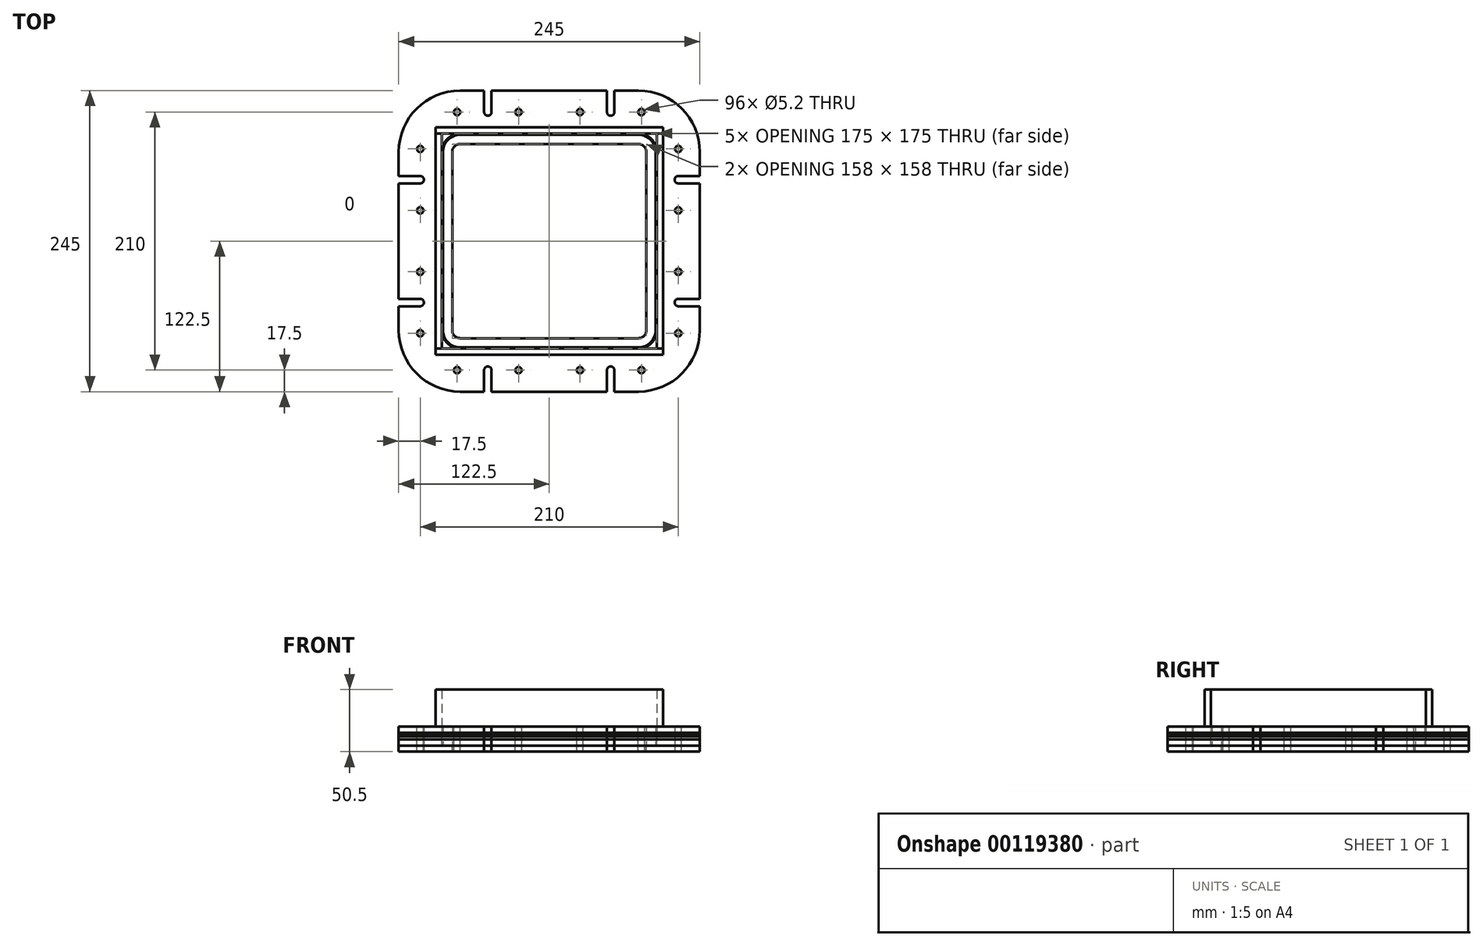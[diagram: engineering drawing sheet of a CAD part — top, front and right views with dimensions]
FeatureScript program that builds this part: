
annotation { "Feature Type Name" : "Feature", "Feature Type Description" : "" }
export const myFeature = defineFeature(function(context is Context, id is Id, definition is map)
    precondition{}
    {
        {
            var Q0;
            Q0=qCreatedBy(makeId("Top.planeOp"),FACE);
            var sketch = newSketch(context, id + "F0", { "sketchPlane" : qUnion([Q0])});
            skLineSegment(sketch, "E0.bottom", {"start": v(72.5, -87.5) * mm, "end": v(-72.5, -87.5) * mm});
            skLineSegment(sketch, "E0.top", {"start": v(72.5, 87.5) * mm, "end": v(-72.5, 87.5) * mm});
            skLineSegment(sketch, "E0.left", {"start": v(87.5, -72.5) * mm, "end": v(87.5, 72.5) * mm});
            skLineSegment(sketch, "E0.right", {"start": v(-87.5, -72.5) * mm, "end": v(-87.5, 72.5) * mm});
            skPoint(sketch, "E0.middle", {"position": v(0, 0) * mm});
            skPoint(sketch, "E1.visualSharp", {"position": v(-87.5, 87.5) * mm});
            skArc(sketch, "E1.filletArc", {"start": v(-72.5, 87.5) * mm, "mid": v(-83.1, 83.1) * mm, "end": v(-87.5, 72.5) * mm});
            skPoint(sketch, "E2.visualSharp", {"position": v(87.5, 87.5) * mm});
            skArc(sketch, "E2.filletArc", {"start": v(87.5, 72.5) * mm, "mid": v(83.1, 83.1) * mm, "end": v(72.5, 87.5) * mm});
            skPoint(sketch, "E3.visualSharp", {"position": v(87.5, -87.5) * mm});
            skArc(sketch, "E3.filletArc", {"start": v(72.5, -87.5) * mm, "mid": v(83.1, -83.1) * mm, "end": v(87.5, -72.5) * mm});
            skPoint(sketch, "E4.visualSharp", {"position": v(-87.5, -87.5) * mm});
            skArc(sketch, "E4.filletArc", {"start": v(-87.5, -72.5) * mm, "mid": v(-83.1, -83.1) * mm, "end": v(-72.5, -87.5) * mm});
            skArc(sketch, "E5.0", {"start": v(72.5, -122.5) * mm, "mid": v(107.86, -107.86) * mm, "end": v(122.5, -72.5) * mm});
            skLineSegment(sketch, "E5.1", {"start": v(72.5, -122.5) * mm, "end": v(-72.5, -122.5) * mm});
            skLineSegment(sketch, "E5.2", {"start": v(122.5, -72.5) * mm, "end": v(122.5, 72.5) * mm});
            skArc(sketch, "E5.3", {"start": v(-122.5, -72.5) * mm, "mid": v(-107.86, -107.86) * mm, "end": v(-72.5, -122.5) * mm});
            skArc(sketch, "E5.4", {"start": v(122.5, 72.5) * mm, "mid": v(107.86, 107.86) * mm, "end": v(72.5, 122.5) * mm});
            skLineSegment(sketch, "E5.5", {"start": v(72.5, 122.5) * mm, "end": v(-72.5, 122.5) * mm});
            skArc(sketch, "E5.6", {"start": v(-72.5, 122.5) * mm, "mid": v(-107.86, 107.86) * mm, "end": v(-122.5, 72.5) * mm});
            skLineSegment(sketch, "E5.7", {"start": v(-122.5, -72.5) * mm, "end": v(-122.5, 72.5) * mm});
            skSolve(sketch);
        }
        {
            var Q0;
            Q0=makeQuery(id+"F0.imprint","IMPRINT",FACE,{"disambiguationData":[TD([[makeQuery(id+"F0.imprint","IMPRINT",EDGE,{"derivedFrom":sQuery(id+"F0.wireOp",EDGE,"E0.bottom")}),1.0]])]});
            extrude(context, id + "F1", {"entities" : qUnion([Q0]), "depth" : 5 * mm});
        }
        {
            var Q0;
            Q0=makeQuery(id+"F1.opExtrude","CAP_FACE",FACE,{"disambiguationData":[OSD([sQuery(id+"F0.wireOp",EDGE,"E0.bottom"),sQuery(id+"F0.wireOp",EDGE,"E0.top"),sQuery(id+"F0.wireOp",EDGE,"E0.left"),sQuery(id+"F0.wireOp",EDGE,"E0.right"),sQuery(id+"F0.wireOp",EDGE,"E1.filletArc"),sQuery(id+"F0.wireOp",EDGE,"E2.filletArc"),sQuery(id+"F0.wireOp",EDGE,"E3.filletArc"),sQuery(id+"F0.wireOp",EDGE,"E4.filletArc"),sQuery(id+"F0.wireOp",EDGE,"E5.0"),sQuery(id+"F0.wireOp",EDGE,"E5.1"),sQuery(id+"F0.wireOp",EDGE,"E5.2"),sQuery(id+"F0.wireOp",EDGE,"E5.3"),sQuery(id+"F0.wireOp",EDGE,"E5.4"),sQuery(id+"F0.wireOp",EDGE,"E5.5"),sQuery(id+"F0.wireOp",EDGE,"E5.6"),sQuery(id+"F0.wireOp",EDGE,"E5.7")])],"isStart":true});
            var sketch = newSketch(context, id + "F2", { "sketchPlane" : qUnion([Q0])});
            skArc(sketch, "E6", {"start": v(72.5, 87.5) * mm, "mid": v(83.1, 83.1) * mm, "end": v(87.5, 72.5) * mm});
            skLineSegment(sketch, "E7", {"start": v(72.5, 87.5) * mm, "end": v(-72.5, 87.5) * mm});
            skArc(sketch, "E8", {"start": v(-87.5, 72.5) * mm, "mid": v(-83.1, 83.1) * mm, "end": v(-72.5, 87.5) * mm});
            skLineSegment(sketch, "E9", {"start": v(-87.5, 72.5) * mm, "end": v(-87.5, -72.5) * mm});
            skArc(sketch, "E10", {"start": v(-72.5, -87.5) * mm, "mid": v(-83.1, -83.1) * mm, "end": v(-87.5, -72.5) * mm});
            skLineSegment(sketch, "E11", {"start": v(72.5, -87.5) * mm, "end": v(-72.5, -87.5) * mm});
            skArc(sketch, "E12", {"start": v(87.5, -72.5) * mm, "mid": v(83.1, -83.1) * mm, "end": v(72.5, -87.5) * mm});
            skLineSegment(sketch, "E13", {"start": v(87.5, 72.5) * mm, "end": v(87.5, -72.5) * mm});
            skArc(sketch, "E14", {"start": v(-122.5, 72.5) * mm, "mid": v(-107.86, 107.86) * mm, "end": v(-72.5, 122.5) * mm});
            skLineSegment(sketch, "E15", {"start": v(-122.5, 72.5) * mm, "end": v(-122.5, -72.5) * mm});
            skArc(sketch, "E16", {"start": v(-72.5, -122.5) * mm, "mid": v(-107.86, -107.86) * mm, "end": v(-122.5, -72.5) * mm});
            skLineSegment(sketch, "E17", {"start": v(72.5, -122.5) * mm, "end": v(-72.5, -122.5) * mm});
            skArc(sketch, "E18", {"start": v(122.5, -72.5) * mm, "mid": v(107.86, -107.86) * mm, "end": v(72.5, -122.5) * mm});
            skLineSegment(sketch, "E19", {"start": v(122.5, 72.5) * mm, "end": v(122.5, -72.5) * mm});
            skArc(sketch, "E20", {"start": v(72.5, 122.5) * mm, "mid": v(107.86, 107.86) * mm, "end": v(122.5, 72.5) * mm});
            skLineSegment(sketch, "E21", {"start": v(72.5, 122.5) * mm, "end": v(-72.5, 122.5) * mm});
            skSolve(sketch);
        }
        {
            var Q0;
            Q0=makeQuery(id+"F2.imprint","IMPRINT",FACE,{"disambiguationData":[TD([[makeQuery(id+"F2.imprint","IMPRINT",EDGE,{"derivedFrom":sQuery(id+"F2.wireOp",EDGE,"41d78850-efe2-4f69-8b8e-5f8f88f08fe800")}),1.0]])]});
            var Q1;
            Q1=makeQuery(id+"F2.imprint","IMPRINT",FACE,{"disambiguationData":[TD([[makeQuery(id+"F2.imprint","IMPRINT",EDGE,{"derivedFrom":sQuery(id+"F2.wireOp",EDGE,"E6")}),1.0]])]});
            extrude(context, id + "F3", {"entities" : qUnion([Q0, Q1]), "depth" : 2.5 * mm});
        }
        {
            var Q0;
            Q0=makeQuery(id+"F1.opExtrude","CAP_FACE",FACE,{"disambiguationData":[OSD([sQuery(id+"F0.wireOp",EDGE,"E0.bottom"),sQuery(id+"F0.wireOp",EDGE,"E0.top"),sQuery(id+"F0.wireOp",EDGE,"E0.left"),sQuery(id+"F0.wireOp",EDGE,"E0.right"),sQuery(id+"F0.wireOp",EDGE,"E1.filletArc"),sQuery(id+"F0.wireOp",EDGE,"E2.filletArc"),sQuery(id+"F0.wireOp",EDGE,"E3.filletArc"),sQuery(id+"F0.wireOp",EDGE,"E4.filletArc"),sQuery(id+"F0.wireOp",EDGE,"E5.0"),sQuery(id+"F0.wireOp",EDGE,"E5.1"),sQuery(id+"F0.wireOp",EDGE,"E5.2"),sQuery(id+"F0.wireOp",EDGE,"E5.3"),sQuery(id+"F0.wireOp",EDGE,"E5.4"),sQuery(id+"F0.wireOp",EDGE,"E5.5"),sQuery(id+"F0.wireOp",EDGE,"E5.6"),sQuery(id+"F0.wireOp",EDGE,"E5.7")])],"isStart":false});
            var sketch = newSketch(context, id + "F4", { "sketchPlane" : qUnion([Q0])});
            skLineSegment(sketch, "E22.bottom", {"start": v(-92.5, -87.5) * mm, "end": v(92.5, -87.5) * mm});
            skLineSegment(sketch, "E22.top", {"start": v(-92.5, 87.5) * mm, "end": v(92.5, 87.5) * mm});
            skLineSegment(sketch, "E22.left", {"start": v(-87.5, -87.5) * mm, "end": v(-87.5, 87.5) * mm});
            skLineSegment(sketch, "E22.right", {"start": v(87.5, -87.5) * mm, "end": v(87.5, 87.5) * mm});
            skPoint(sketch, "E22.middle", {"position": v(0, 0) * mm});
            skLineSegment(sketch, "E23.0", {"start": v(-92.5, -92.5) * mm, "end": v(92.5, -92.5) * mm});
            skLineSegment(sketch, "E23.1", {"start": v(-92.5, -92.5) * mm, "end": v(-92.5, 92.5) * mm});
            skLineSegment(sketch, "E23.2", {"start": v(-92.5, 92.5) * mm, "end": v(92.5, 92.5) * mm});
            skLineSegment(sketch, "E23.3", {"start": v(92.5, -92.5) * mm, "end": v(92.5, 92.5) * mm});
            skSolve(sketch);
        }
        {
            var Q0;
            {var subQ5=sQuery(id+"F4.wireOp",EDGE,"E23.2");Q0=makeQuery(id+"F4.imprint","IMPRINT",FACE,{"disambiguationData":[TD([[makeQuery(id+"F4.imprint","IMPRINT",EDGE,{"derivedFrom":subQ5}),-1.0]])]});}
            var Q1;
            {var subQ4=sQuery(id+"F4.wireOp",EDGE,"E23.0");Q1=makeQuery(id+"F4.imprint","IMPRINT",FACE,{"disambiguationData":[TD([[makeQuery(id+"F4.imprint","IMPRINT",EDGE,{"derivedFrom":subQ4}),1.0]])]});}
            extrude(context, id + "F5", {"entities" : qUnion([Q0, Q1]), "depth" : 30 * mm});
        }
        {
            var Q0;
            Q0=makeQuery(id+"F1.opExtrude","CAP_FACE",FACE,{"disambiguationData":[OSD([sQuery(id+"F0.wireOp",EDGE,"E0.bottom"),sQuery(id+"F0.wireOp",EDGE,"E0.top"),sQuery(id+"F0.wireOp",EDGE,"E0.left"),sQuery(id+"F0.wireOp",EDGE,"E0.right"),sQuery(id+"F0.wireOp",EDGE,"E1.filletArc"),sQuery(id+"F0.wireOp",EDGE,"E2.filletArc"),sQuery(id+"F0.wireOp",EDGE,"E3.filletArc"),sQuery(id+"F0.wireOp",EDGE,"E4.filletArc"),sQuery(id+"F0.wireOp",EDGE,"E5.0"),sQuery(id+"F0.wireOp",EDGE,"E5.1"),sQuery(id+"F0.wireOp",EDGE,"E5.2"),sQuery(id+"F0.wireOp",EDGE,"E5.3"),sQuery(id+"F0.wireOp",EDGE,"E5.4"),sQuery(id+"F0.wireOp",EDGE,"E5.5"),sQuery(id+"F0.wireOp",EDGE,"E5.6"),sQuery(id+"F0.wireOp",EDGE,"E5.7")])],"isStart":false});
            var sketch = newSketch(context, id + "F6", { "sketchPlane" : qUnion([Q0])});
            skLineSegment(sketch, "E24.bottom", {"start": v(87.5, 87.5) * mm, "end": v(92.5, 87.5) * mm});
            skLineSegment(sketch, "E24.top", {"start": v(87.5, -87.5) * mm, "end": v(92.5, -87.5) * mm});
            skLineSegment(sketch, "E24.left", {"start": v(87.5, 87.5) * mm, "end": v(87.5, -87.5) * mm});
            skLineSegment(sketch, "E24.right", {"start": v(92.5, 87.5) * mm, "end": v(92.5, -87.5) * mm});
            skLineSegment(sketch, "E25.bottom", {"start": v(-87.5, 87.5) * mm, "end": v(-92.5, 87.5) * mm});
            skLineSegment(sketch, "E25.top", {"start": v(-87.5, -87.5) * mm, "end": v(-92.5, -87.5) * mm});
            skLineSegment(sketch, "E25.left", {"start": v(-87.5, 87.5) * mm, "end": v(-87.5, -87.5) * mm});
            skLineSegment(sketch, "E25.right", {"start": v(-92.5, 87.5) * mm, "end": v(-92.5, -87.5) * mm});
            skSolve(sketch);
        }
        {
            var Q0;
            {var subQ3=sQuery(id+"F6.wireOp",EDGE,"E25.bottom");Q0=makeQuery(id+"F6.imprint","IMPRINT",FACE,{"disambiguationData":[TD([[makeQuery(id+"F6.imprint","IMPRINT",EDGE,{"derivedFrom":subQ3}),1.0]])]});}
            var Q1;
            {var subQ4=sQuery(id+"F6.wireOp",EDGE,"E24.bottom");Q1=makeQuery(id+"F6.imprint","IMPRINT",FACE,{"disambiguationData":[TD([[makeQuery(id+"F6.imprint","IMPRINT",EDGE,{"derivedFrom":subQ4}),-1.0]])]});}
            extrude(context, id + "F7", {"entities" : qUnion([Q0, Q1]), "depth" : 30 * mm});
        }
        {
            var Q0;
            Q0=makeQuery(id+"F3.opExtrude","CAP_FACE",FACE,{"disambiguationData":[OSD([sQuery(id+"F2.wireOp",EDGE,"E6"),sQuery(id+"F2.wireOp",EDGE,"E7"),sQuery(id+"F2.wireOp",EDGE,"E8"),sQuery(id+"F2.wireOp",EDGE,"E9"),sQuery(id+"F2.wireOp",EDGE,"E10"),sQuery(id+"F2.wireOp",EDGE,"E11"),sQuery(id+"F2.wireOp",EDGE,"E12"),sQuery(id+"F2.wireOp",EDGE,"E13"),sQuery(id+"F2.wireOp",EDGE,"E14"),sQuery(id+"F2.wireOp",EDGE,"E15"),sQuery(id+"F2.wireOp",EDGE,"E16"),sQuery(id+"F2.wireOp",EDGE,"E17"),sQuery(id+"F2.wireOp",EDGE,"E18"),sQuery(id+"F2.wireOp",EDGE,"E19"),sQuery(id+"F2.wireOp",EDGE,"E20"),sQuery(id+"F2.wireOp",EDGE,"E21")])],"isStart":false});
            extrude(context, id + "F8", {"entities" : qUnion([Q0]), "depth" : .5 * mm});
        }
        {
            var Q0;
            Q0=makeQuery(id+"F8.opExtrude","CAP_FACE",FACE,{"disambiguationData":[OSD([sQuery(id+"F2.wireOp",EDGE,"E6"),sQuery(id+"F2.wireOp",EDGE,"E7"),sQuery(id+"F2.wireOp",EDGE,"E8"),sQuery(id+"F2.wireOp",EDGE,"E9"),sQuery(id+"F2.wireOp",EDGE,"E10"),sQuery(id+"F2.wireOp",EDGE,"E11"),sQuery(id+"F2.wireOp",EDGE,"E12"),sQuery(id+"F2.wireOp",EDGE,"E13"),sQuery(id+"F2.wireOp",EDGE,"E14"),sQuery(id+"F2.wireOp",EDGE,"E15"),sQuery(id+"F2.wireOp",EDGE,"E16"),sQuery(id+"F2.wireOp",EDGE,"E17"),sQuery(id+"F2.wireOp",EDGE,"E18"),sQuery(id+"F2.wireOp",EDGE,"E19"),sQuery(id+"F2.wireOp",EDGE,"E20"),sQuery(id+"F2.wireOp",EDGE,"E21")])],"isStart":false});
            extrude(context, id + "F9", {"entities" : qUnion([Q0]), "depth" : 2.5 * mm});
        }
        {
            var Q0;
            Q0=makeQuery(id+"F9.opExtrude","CAP_FACE",FACE,{"disambiguationData":[OSD([sQuery(id+"F2.wireOp",EDGE,"E6"),sQuery(id+"F2.wireOp",EDGE,"E7"),sQuery(id+"F2.wireOp",EDGE,"E8"),sQuery(id+"F2.wireOp",EDGE,"E9"),sQuery(id+"F2.wireOp",EDGE,"E10"),sQuery(id+"F2.wireOp",EDGE,"E11"),sQuery(id+"F2.wireOp",EDGE,"E12"),sQuery(id+"F2.wireOp",EDGE,"E13"),sQuery(id+"F2.wireOp",EDGE,"E14"),sQuery(id+"F2.wireOp",EDGE,"E15"),sQuery(id+"F2.wireOp",EDGE,"E16"),sQuery(id+"F2.wireOp",EDGE,"E17"),sQuery(id+"F2.wireOp",EDGE,"E18"),sQuery(id+"F2.wireOp",EDGE,"E19"),sQuery(id+"F2.wireOp",EDGE,"E20"),sQuery(id+"F2.wireOp",EDGE,"E21")])],"isStart":false});
            extrude(context, id + "F10", {"entities" : qUnion([Q0]), "depth" : 5 * mm});
        }
        {
            var Q0;
            Q0=makeQuery(id+"F10.opExtrude","CAP_FACE",FACE,{"disambiguationData":[OSD([sQuery(id+"F2.wireOp",EDGE,"E6"),sQuery(id+"F2.wireOp",EDGE,"E7"),sQuery(id+"F2.wireOp",EDGE,"E8"),sQuery(id+"F2.wireOp",EDGE,"E9"),sQuery(id+"F2.wireOp",EDGE,"E10"),sQuery(id+"F2.wireOp",EDGE,"E11"),sQuery(id+"F2.wireOp",EDGE,"E12"),sQuery(id+"F2.wireOp",EDGE,"E13"),sQuery(id+"F2.wireOp",EDGE,"E14"),sQuery(id+"F2.wireOp",EDGE,"E15"),sQuery(id+"F2.wireOp",EDGE,"E16"),sQuery(id+"F2.wireOp",EDGE,"E17"),sQuery(id+"F2.wireOp",EDGE,"E18"),sQuery(id+"F2.wireOp",EDGE,"E19"),sQuery(id+"F2.wireOp",EDGE,"E20"),sQuery(id+"F2.wireOp",EDGE,"E21")])],"isStart":false});
            var sketch = newSketch(context, id + "F11", { "sketchPlane" : qUnion([Q0])});
            skLineSegment(sketch, "E26.0", {"start": v(72.5, 86.5) * mm, "end": v(-72.5, 86.5) * mm});
            skArc(sketch, "E26.1", {"start": v(-86.5, 72.5) * mm, "mid": v(-82.4, 82.4) * mm, "end": v(-72.5, 86.5) * mm});
            skArc(sketch, "E26.2", {"start": v(72.5, 86.5) * mm, "mid": v(82.4, 82.4) * mm, "end": v(86.5, 72.5) * mm});
            skLineSegment(sketch, "E26.3", {"start": v(-86.5, 72.5) * mm, "end": v(-86.5, -72.5) * mm});
            skLineSegment(sketch, "E26.4", {"start": v(86.5, 72.5) * mm, "end": v(86.5, -72.5) * mm});
            skArc(sketch, "E26.5", {"start": v(86.5, -72.5) * mm, "mid": v(82.4, -82.4) * mm, "end": v(72.5, -86.5) * mm});
            skLineSegment(sketch, "E26.6", {"start": v(72.5, -86.5) * mm, "end": v(-72.5, -86.5) * mm});
            skArc(sketch, "E26.7", {"start": v(-72.5, -86.5) * mm, "mid": v(-82.4, -82.4) * mm, "end": v(-86.5, -72.5) * mm});
            skLineSegment(sketch, "E27.0", {"start": v(72.5, 79) * mm, "end": v(-72.5, 79) * mm});
            skArc(sketch, "E27.1", {"start": v(-79, 72.5) * mm, "mid": v(-77.1, 77.1) * mm, "end": v(-72.5, 79) * mm});
            skArc(sketch, "E27.2", {"start": v(72.5, 79) * mm, "mid": v(77.1, 77.1) * mm, "end": v(79, 72.5) * mm});
            skLineSegment(sketch, "E27.3", {"start": v(-79, 72.5) * mm, "end": v(-79, -72.5) * mm});
            skLineSegment(sketch, "E27.4", {"start": v(79, 72.5) * mm, "end": v(79, -72.5) * mm});
            skArc(sketch, "E27.5", {"start": v(79, -72.5) * mm, "mid": v(77.1, -77.1) * mm, "end": v(72.5, -79) * mm});
            skLineSegment(sketch, "E27.6", {"start": v(72.5, -79) * mm, "end": v(-72.5, -79) * mm});
            skArc(sketch, "E27.7", {"start": v(-72.5, -79) * mm, "mid": v(-77.1, -77.1) * mm, "end": v(-79, -72.5) * mm});
            skLineSegment(sketch, "E28.0", {"start": v(72.5, 122.5) * mm, "end": v(-72.5, 122.5) * mm});
            skArc(sketch, "E29.0", {"start": v(-122.5, 72.5) * mm, "mid": v(-107.86, 107.86) * mm, "end": v(-72.5, 122.5) * mm});
            skLineSegment(sketch, "E30.0", {"start": v(-122.5, 72.5) * mm, "end": v(-122.5, -72.5) * mm});
            skArc(sketch, "E31.0", {"start": v(-72.5, -122.5) * mm, "mid": v(-107.86, -107.86) * mm, "end": v(-122.5, -72.5) * mm});
            skLineSegment(sketch, "E32.0", {"start": v(72.5, -122.5) * mm, "end": v(-72.5, -122.5) * mm});
            skArc(sketch, "E33.0", {"start": v(122.5, -72.5) * mm, "mid": v(107.86, -107.86) * mm, "end": v(72.5, -122.5) * mm});
            skLineSegment(sketch, "E34.0", {"start": v(122.5, 72.5) * mm, "end": v(122.5, -72.5) * mm});
            skArc(sketch, "E35.0", {"start": v(72.5, 122.5) * mm, "mid": v(107.86, 107.86) * mm, "end": v(122.5, 72.5) * mm});
            skSolve(sketch);
        }
        {
            var Q0;
            Q0=makeQuery(id+"F11.imprint","IMPRINT",FACE,{"disambiguationData":[TD([[makeQuery(id+"F11.imprint","IMPRINT",EDGE,{"derivedFrom":sQuery(id+"F11.wireOp",EDGE,"E26.0")}),1.0]])]});
            extrude(context, id + "F12", {"entities" : qUnion([Q0]), "oppositeDirection" : true, "depth" : 15 * mm});
        }
        {
            var Q0;
            Q0 = qSketchRegion(id + "F11", true);
            var Q1;
            Q1=makeQuery(id+"F11.imprint","IMPRINT",FACE,{"disambiguationData":[TD([[makeQuery(id+"F11.imprint","IMPRINT",EDGE,{"derivedFrom":sQuery(id+"F11.wireOp",EDGE,"E26.0")}),1.0]])]});
            extrude(context, id + "F13", {"entities" : qUnion([Q0, Q1]), "depth" : 5 * mm});
        }
        {
            var Q0;
            Q0=makeQuery(id+"F13.opExtrude","CAP_FACE",FACE,{"disambiguationData":[OSD([sQuery(id+"F11.wireOp",EDGE,"E27.0"),sQuery(id+"F11.wireOp",EDGE,"E27.1"),sQuery(id+"F11.wireOp",EDGE,"E27.2"),sQuery(id+"F11.wireOp",EDGE,"E27.3"),sQuery(id+"F11.wireOp",EDGE,"E27.4"),sQuery(id+"F11.wireOp",EDGE,"E27.5"),sQuery(id+"F11.wireOp",EDGE,"E27.6"),sQuery(id+"F11.wireOp",EDGE,"E27.7"),sQuery(id+"F11.wireOp",EDGE,"E28.0"),sQuery(id+"F11.wireOp",EDGE,"E29.0"),sQuery(id+"F11.wireOp",EDGE,"E30.0"),sQuery(id+"F11.wireOp",EDGE,"E31.0"),sQuery(id+"F11.wireOp",EDGE,"E32.0"),sQuery(id+"F11.wireOp",EDGE,"E33.0"),sQuery(id+"F11.wireOp",EDGE,"E34.0"),sQuery(id+"F11.wireOp",EDGE,"E35.0")])],"isStart":false});
            var sketch = newSketch(context, id + "F14", { "sketchPlane" : qUnion([Q0])});
            skLineSegment(sketch, "E36.bottom", {"start": v(105, -105) * mm, "end": v(-105, -105) * mm, "construction": true});
            skLineSegment(sketch, "E36.top", {"start": v(105, 105) * mm, "end": v(-105, 105) * mm, "construction": true});
            skLineSegment(sketch, "E36.left", {"start": v(105, -105) * mm, "end": v(105, -53) * mm, "construction": true});
            skLineSegment(sketch, "E36.right", {"start": v(-105, -105) * mm, "end": v(-105, -53) * mm, "construction": true});
            skPoint(sketch, "E36.middle", {"position": v(0, 0) * mm});
            skPoint(sketch, "E37.1.0.0", {"position": v(50, 105) * mm});
            skPoint(sketch, "E37.1.1.0", {"position": v(50, -105) * mm});
            skLineSegment(sketch, "E37.direction1", {"start": v(0, 105) * mm, "end": v(50, 105) * mm, "construction": true});
            skLineSegment(sketch, "E37.direction2", {"start": v(0, 105) * mm, "end": v(0, -105) * mm, "construction": true});
            skPoint(sketch, "E38.MirrorP", {"position": v(-50, -105) * mm});
            skPoint(sketch, "E39.MirrorP", {"position": v(-50, 105) * mm});
            skPoint(sketch, "E40.0.1.0", {"position": v(-105, 50) * mm});
            skPoint(sketch, "E40.1.1.0", {"position": v(105, 50) * mm});
            skLineSegment(sketch, "E40.direction1", {"start": v(-105, 0) * mm, "end": v(105, 0) * mm, "construction": true});
            skLineSegment(sketch, "E40.direction2", {"start": v(-105, 0) * mm, "end": v(-105, 50) * mm, "construction": true});
            skPoint(sketch, "E41.MirrorP", {"position": v(-105, -50) * mm});
            skPoint(sketch, "E42.MirrorP", {"position": v(105, -50) * mm});
            skArc(sketch, "E43", {"start": v(-53, 105) * mm, "mid": v(-50, 102) * mm, "end": v(-47, 105) * mm});
            skArc(sketch, "E44", {"start": v(47, 105) * mm, "mid": v(50, 102) * mm, "end": v(53, 105) * mm});
            skArc(sketch, "E45", {"start": v(105, 53) * mm, "mid": v(102, 50) * mm, "end": v(105, 47) * mm});
            skArc(sketch, "E46", {"start": v(-105, 47) * mm, "mid": v(-102, 50) * mm, "end": v(-105, 53) * mm});
            skArc(sketch, "E47", {"start": v(-105, -53) * mm, "mid": v(-102, -50) * mm, "end": v(-105, -47) * mm});
            skArc(sketch, "E48", {"start": v(105, -47) * mm, "mid": v(102, -50) * mm, "end": v(105, -53) * mm});
            skArc(sketch, "E49", {"start": v(53, -105) * mm, "mid": v(50, -102) * mm, "end": v(47, -105) * mm});
            skArc(sketch, "E50", {"start": v(-47, -105) * mm, "mid": v(-50, -102) * mm, "end": v(-53, -105) * mm});
            skLineSegment(sketch, "E51.bottom", {"start": v(105, -47) * mm, "end": v(130.46, -47) * mm});
            skLineSegment(sketch, "E51.top", {"start": v(105, -53) * mm, "end": v(130.46, -53) * mm});
            skLineSegment(sketch, "E51.right", {"start": v(130.46, -47) * mm, "end": v(130.46, -53) * mm});
            skLineSegment(sketch, "E52.bottom", {"start": v(105, 53) * mm, "end": v(126.53, 53) * mm});
            skLineSegment(sketch, "E52.top", {"start": v(105, 47) * mm, "end": v(126.53, 47) * mm});
            skLineSegment(sketch, "E52.right", {"start": v(126.53, 53) * mm, "end": v(126.53, 47) * mm});
            skLineSegment(sketch, "E53.trimOffspring", {"start": v(105, 53) * mm, "end": v(105, 105) * mm, "construction": true});
            skLineSegment(sketch, "E54.trimOffspring", {"start": v(105, -47) * mm, "end": v(105, 47) * mm, "construction": true});
            skLineSegment(sketch, "E55.bottom", {"start": v(-105, -47) * mm, "end": v(-130.07, -47) * mm});
            skLineSegment(sketch, "E55.top", {"start": v(-105, -53) * mm, "end": v(-130.07, -53) * mm});
            skLineSegment(sketch, "E55.right", {"start": v(-130.07, -47) * mm, "end": v(-130.07, -53) * mm});
            skLineSegment(sketch, "E56", {"start": v(-105, 53) * mm, "end": v(-128.49, 53) * mm});
            skLineSegment(sketch, "E57", {"start": v(-105, 47) * mm, "end": v(-126.24, 47) * mm});
            skLineSegment(sketch, "E58", {"start": v(-126.24, 47.03) * mm, "end": v(-128.49, 53) * mm});
            skLineSegment(sketch, "E59.trimOffspring", {"start": v(-105, -47) * mm, "end": v(-105, 105) * mm, "construction": true});
            skLineSegment(sketch, "E60", {"start": v(-53, -105) * mm, "end": v(-53, -131.37) * mm});
            skLineSegment(sketch, "E61", {"start": v(-47, -105) * mm, "end": v(-47, -130.85) * mm});
            skLineSegment(sketch, "E62", {"start": v(47, -105) * mm, "end": v(47, -132.23) * mm});
            skLineSegment(sketch, "E63", {"start": v(53, -105) * mm, "end": v(53, -133.09) * mm});
            skLineSegment(sketch, "E64", {"start": v(53, -133.09) * mm, "end": v(47, -132.23) * mm});
            skLineSegment(sketch, "E65", {"start": v(-47, -130.85) * mm, "end": v(-53, -131.37) * mm});
            skLineSegment(sketch, "E66", {"start": v(-47, 105) * mm, "end": v(-47, 133.72) * mm});
            skLineSegment(sketch, "E67", {"start": v(-53, 105) * mm, "end": v(-53, 134.9) * mm});
            skLineSegment(sketch, "E68", {"start": v(47, 105) * mm, "end": v(47, 134.1) * mm});
            skLineSegment(sketch, "E69", {"start": v(53, 105) * mm, "end": v(53, 135.1) * mm});
            skLineSegment(sketch, "E70", {"start": v(53, 135.1) * mm, "end": v(47, 134.1) * mm});
            skLineSegment(sketch, "E71", {"start": v(-47, 133.72) * mm, "end": v(-53, 134.9) * mm});
            skSolve(sketch);
        }
        {
            var Q0;
            {var subQ0=sQuery(id+"F14.wireOp",EDGE,"E44");Q0=makeQuery(id+"F14.imprint","IMPRINT",FACE,{"disambiguationData":[TD([[makeQuery(id+"F14.imprint","IMPRINT",EDGE,{"derivedFrom":subQ0}),1.0]])]});}
            var Q1;
            {var subQ0=sQuery(id+"F14.wireOp",EDGE,"E70");Q1=makeQuery(id+"F14.imprint","IMPRINT",FACE,{"disambiguationData":[TD([[makeQuery(id+"F14.imprint","IMPRINT",EDGE,{"derivedFrom":subQ0}),1.0]])]});}
            var Q2;
            {var subQ0=sQuery(id+"F14.wireOp",EDGE,"E71");Q2=makeQuery(id+"F14.imprint","IMPRINT",FACE,{"disambiguationData":[TD([[makeQuery(id+"F14.imprint","IMPRINT",EDGE,{"derivedFrom":subQ0}),1.0]])]});}
            var Q3;
            {var subQ0=sQuery(id+"F14.wireOp",EDGE,"E43");Q3=makeQuery(id+"F14.imprint","IMPRINT",FACE,{"disambiguationData":[TD([[makeQuery(id+"F14.imprint","IMPRINT",EDGE,{"derivedFrom":subQ0}),1.0]])]});}
            var Q4;
            {var subQ0=sQuery(id+"F14.wireOp",EDGE,"E46");Q4=makeQuery(id+"F14.imprint","IMPRINT",FACE,{"disambiguationData":[TD([[makeQuery(id+"F14.imprint","IMPRINT",EDGE,{"derivedFrom":subQ0}),1.0]])]});}
            var Q5;
            {var subQ0=sQuery(id+"F14.wireOp",EDGE,"E47");Q5=makeQuery(id+"F14.imprint","IMPRINT",FACE,{"disambiguationData":[TD([[makeQuery(id+"F14.imprint","IMPRINT",EDGE,{"derivedFrom":subQ0}),1.0]])]});}
            var Q6;
            {var subQ0=sQuery(id+"F14.wireOp",EDGE,"E50");Q6=makeQuery(id+"F14.imprint","IMPRINT",FACE,{"disambiguationData":[TD([[makeQuery(id+"F14.imprint","IMPRINT",EDGE,{"derivedFrom":subQ0}),1.0]])]});}
            var Q7;
            {var subQ0=sQuery(id+"F14.wireOp",EDGE,"E49");Q7=makeQuery(id+"F14.imprint","IMPRINT",FACE,{"disambiguationData":[TD([[makeQuery(id+"F14.imprint","IMPRINT",EDGE,{"derivedFrom":subQ0}),1.0]])]});}
            var Q8;
            {var subQ0=sQuery(id+"F14.wireOp",EDGE,"E48");Q8=makeQuery(id+"F14.imprint","IMPRINT",FACE,{"disambiguationData":[TD([[makeQuery(id+"F14.imprint","IMPRINT",EDGE,{"derivedFrom":subQ0}),1.0]])]});}
            var Q9;
            {var subQ0=sQuery(id+"F14.wireOp",EDGE,"E45");Q9=makeQuery(id+"F14.imprint","IMPRINT",FACE,{"disambiguationData":[TD([[makeQuery(id+"F14.imprint","IMPRINT",EDGE,{"derivedFrom":subQ0}),1.0]])]});}
            extrude(context, id + "F15", {"entities" : qUnion([Q0, Q1, Q2, Q3, Q4, Q5, Q6, Q7, Q8, Q9]), "operationType" : NewBodyOperationType.REMOVE, "oppositeDirection" : true, "depth" : 25 * mm});
        }
        {
            var Q0;
            Q0=makeQuery(id+"F1.opExtrude","CAP_FACE",FACE,{"disambiguationData":[OSD([sQuery(id+"F0.wireOp",EDGE,"E0.bottom"),sQuery(id+"F0.wireOp",EDGE,"E0.top"),sQuery(id+"F0.wireOp",EDGE,"E0.left"),sQuery(id+"F0.wireOp",EDGE,"E0.right"),sQuery(id+"F0.wireOp",EDGE,"E1.filletArc"),sQuery(id+"F0.wireOp",EDGE,"E2.filletArc"),sQuery(id+"F0.wireOp",EDGE,"E3.filletArc"),sQuery(id+"F0.wireOp",EDGE,"E4.filletArc"),sQuery(id+"F0.wireOp",EDGE,"E5.0"),sQuery(id+"F0.wireOp",EDGE,"E5.1"),sQuery(id+"F0.wireOp",EDGE,"E5.2"),sQuery(id+"F0.wireOp",EDGE,"E5.3"),sQuery(id+"F0.wireOp",EDGE,"E5.4"),sQuery(id+"F0.wireOp",EDGE,"E5.5"),sQuery(id+"F0.wireOp",EDGE,"E5.6"),sQuery(id+"F0.wireOp",EDGE,"E5.7")])],"isStart":false});
            var sketch = newSketch(context, id + "F16", { "sketchPlane" : qUnion([Q0])});
            skLineSegment(sketch, "E72.bottom", {"start": v(105, -105) * mm, "end": v(-105, -105) * mm, "construction": true});
            skLineSegment(sketch, "E72.top", {"start": v(105, 105) * mm, "end": v(-105, 105) * mm, "construction": true});
            skLineSegment(sketch, "E72.left", {"start": v(105, -105) * mm, "end": v(105, 105) * mm, "construction": true});
            skLineSegment(sketch, "E72.right", {"start": v(-105, -105) * mm, "end": v(-105, 105) * mm, "construction": true});
            skPoint(sketch, "E72.middle", {"position": v(0, 0) * mm});
            skLineSegment(sketch, "E73", {"start": v(-122.5, 0) * mm, "end": v(122.5, 0) * mm, "construction": true});
            skLineSegment(sketch, "E74", {"start": v(0, 122.5) * mm, "end": v(0, -122.5) * mm, "construction": true});
            skCircle(sketch, "E75", {"center": v(-105, 25) * mm, "radius": 2.6 * mm});
            skCircle(sketch, "E76", {"center": v(-105, 75) * mm, "radius": 2.6 * mm});
            skCircle(sketch, "E77", {"center": v(-105, -75) * mm, "radius": 2.6 * mm});
            skCircle(sketch, "E78", {"center": v(-105, -25) * mm, "radius": 2.6 * mm});
            skCircle(sketch, "E79.1.0.0", {"center": v(105, 75) * mm, "radius": 2.6 * mm});
            skCircle(sketch, "E79.1.0.1", {"center": v(105, 25) * mm, "radius": 2.6 * mm});
            skCircle(sketch, "E79.1.0.2", {"center": v(105, -25) * mm, "radius": 2.6 * mm});
            skCircle(sketch, "E79.1.0.3", {"center": v(105, -75) * mm, "radius": 2.6 * mm});
            skLineSegment(sketch, "E79.direction1", {"start": v(-105, 75) * mm, "end": v(105, 75) * mm, "construction": true});
            skCircle(sketch, "E80", {"center": v(-25, -105) * mm, "radius": 2.6 * mm});
            skCircle(sketch, "E81", {"center": v(25, -105) * mm, "radius": 2.6 * mm});
            skCircle(sketch, "E82", {"center": v(75, -105) * mm, "radius": 2.6 * mm});
            skCircle(sketch, "E83", {"center": v(-75, -105) * mm, "radius": 2.6 * mm});
            skCircle(sketch, "E84.0.1.0", {"center": v(-75, 105) * mm, "radius": 2.6 * mm});
            skCircle(sketch, "E84.0.1.1", {"center": v(-25, 105) * mm, "radius": 2.6 * mm});
            skCircle(sketch, "E84.0.1.2", {"center": v(25, 105) * mm, "radius": 2.6 * mm});
            skCircle(sketch, "E84.0.1.3", {"center": v(75, 105) * mm, "radius": 2.6 * mm});
            skLineSegment(sketch, "E84.direction1", {"start": v(-75, -105) * mm, "end": v(-50, -105) * mm, "construction": true});
            skLineSegment(sketch, "E84.direction2", {"start": v(-75, -105) * mm, "end": v(-75, 105) * mm, "construction": true});
            skSolve(sketch);
        }
        {
            var Q0;
            Q0 = qSketchRegion(id + "F16", true);
            extrude(context, id + "F17", {"entities" : qUnion([Q0]), "operationType" : NewBodyOperationType.REMOVE, "endBound" : BoundingType.THROUGH_ALL, "oppositeDirection" : true, "depth" : 25 * mm});
        }
    });
